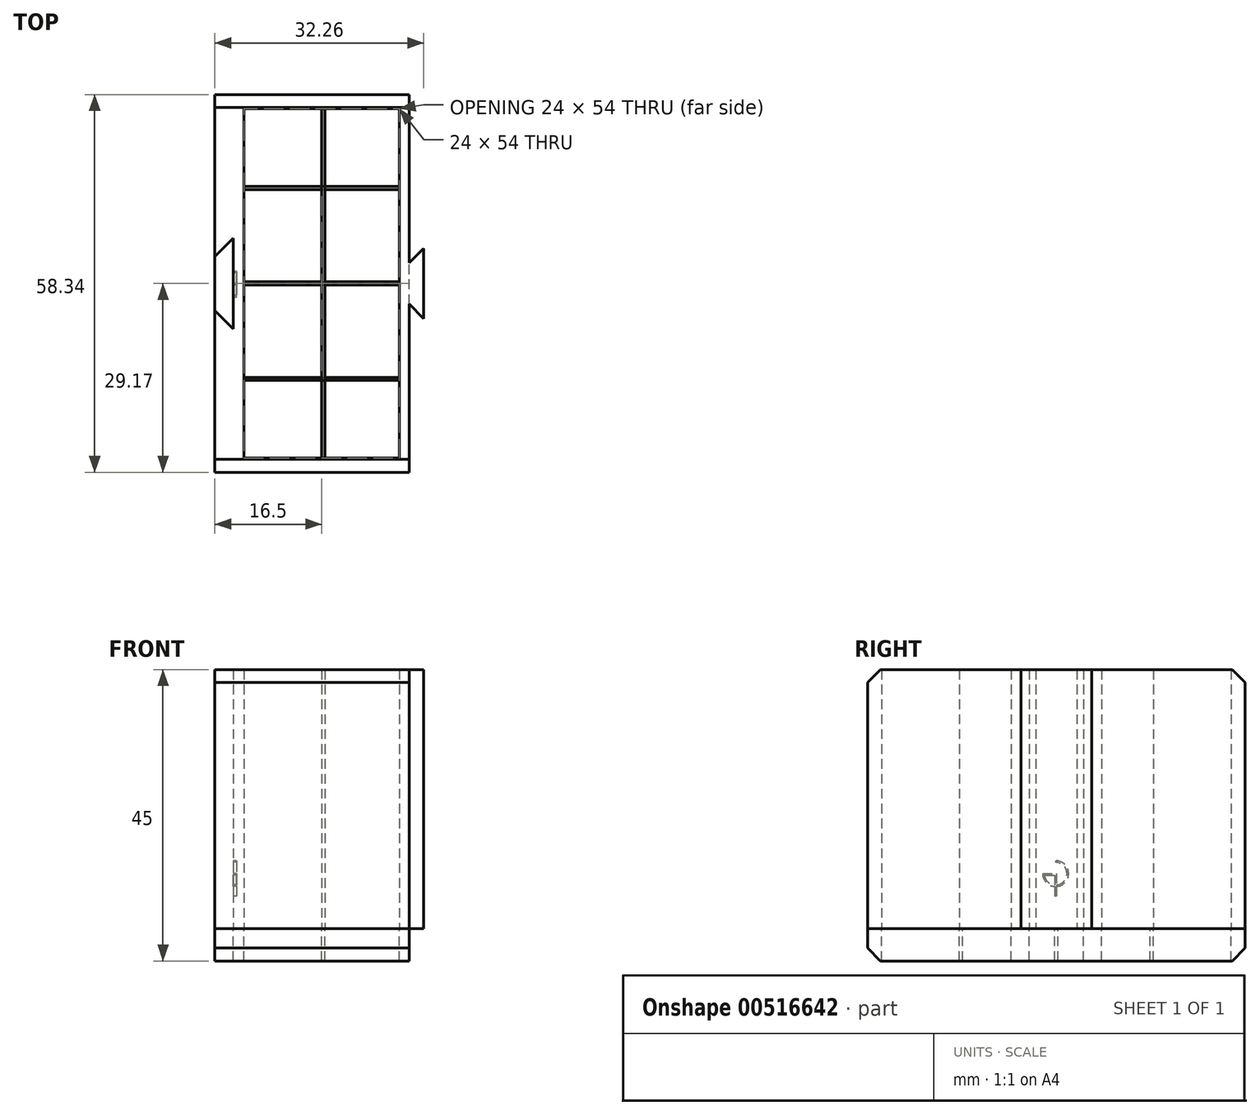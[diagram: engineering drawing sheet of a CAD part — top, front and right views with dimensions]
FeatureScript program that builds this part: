
annotation { "Feature Type Name" : "Feature", "Feature Type Description" : "" }
export const myFeature = defineFeature(function(context is Context, id is Id, definition is map)
    precondition{}
    {
        {
            var Q0;
            Q0=qCreatedBy(makeId("Top.planeOp"),FACE);
            var sketch = newSketch(context, id + "F0", { "sketchPlane" : qUnion([Q0])});
            skLineSegment(sketch, "E0", {"start": v(-15, 4.17) * mm, "end": v(-15, 29.17) * mm});
            skLineSegment(sketch, "E1", {"start": v(-15, 29.17) * mm, "end": v(15, 29.17) * mm});
            skLineSegment(sketch, "E2", {"start": v(15, 29.17) * mm, "end": v(15, 3.17) * mm});
            skLineSegment(sketch, "E3", {"start": v(-15, 4.17) * mm, "end": v(-12.17, 7) * mm});
            skLineSegment(sketch, "E4", {"start": v(-12.17, 7) * mm, "end": v(-12.17, 0) * mm});
            skLineSegment(sketch, "E5", {"start": v(15, 3.17) * mm, "end": v(17.26, 5.43) * mm});
            skLineSegment(sketch, "E6", {"start": v(17.26, 5.43) * mm, "end": v(17.26, -0.57) * mm});
            skLineSegment(sketch, "E7.MirrorCS", {"start": v(-15, -4.17) * mm, "end": v(-12.17, -7) * mm});
            skLineSegment(sketch, "E8.MirrorCS", {"start": v(15, -29.17) * mm, "end": v(15, -3.17) * mm});
            skLineSegment(sketch, "E9.MirrorCS", {"start": v(-12.17, -7) * mm, "end": v(-12.17, 0) * mm});
            skLineSegment(sketch, "E10.MirrorCS", {"start": v(-15, -4.17) * mm, "end": v(-15, -29.17) * mm});
            skLineSegment(sketch, "E11.MirrorCS", {"start": v(17.26, -5.43) * mm, "end": v(17.26, 0.57) * mm});
            skLineSegment(sketch, "E12.MirrorCS", {"start": v(15, -3.17) * mm, "end": v(17.26, -5.43) * mm});
            skLineSegment(sketch, "E13.MirrorCS", {"start": v(-15, -29.17) * mm, "end": v(15, -29.17) * mm});
            skLineSegment(sketch, "E14.bottom", {"start": v(-10.5, 27) * mm, "end": v(13.5, 27) * mm});
            skLineSegment(sketch, "E14.top", {"start": v(-10.5, -27) * mm, "end": v(13.5, -27) * mm});
            skLineSegment(sketch, "E14.left", {"start": v(-10.5, 27) * mm, "end": v(-10.5, -27) * mm});
            skLineSegment(sketch, "E14.right", {"start": v(13.5, 27) * mm, "end": v(13.5, -27) * mm});
            skPoint(sketch, "E14.middle", {"position": v(4, -0.5) * mm});
            skLineSegment(sketch, "E15", {"start": v(-15, 4.17) * mm, "end": v(-15, -4.17) * mm});
            skLineSegment(sketch, "E16", {"start": v(15, -3.17) * mm, "end": v(15, 3.17) * mm});
            skLineSegment(sketch, "E17.bottom", {"start": v(-10.5, 15) * mm, "end": v(13.5, 15) * mm});
            skLineSegment(sketch, "E17.top", {"start": v(-10.5, 14.5) * mm, "end": v(13.5, 14.5) * mm});
            skLineSegment(sketch, "E17.left", {"start": v(-10.5, 15) * mm, "end": v(-10.5, 14.5) * mm});
            skLineSegment(sketch, "E17.right", {"start": v(13.5, 15) * mm, "end": v(13.5, 14.5) * mm});
            skLineSegment(sketch, "E18.bottom", {"start": v(-10.5, -14.5) * mm, "end": v(13.5, -14.5) * mm});
            skLineSegment(sketch, "E18.top", {"start": v(-10.5, -15) * mm, "end": v(13.5, -15) * mm});
            skLineSegment(sketch, "E18.left", {"start": v(-10.5, -14.5) * mm, "end": v(-10.5, -15) * mm});
            skLineSegment(sketch, "E18.right", {"start": v(13.5, -14.5) * mm, "end": v(13.5, -15) * mm});
            skLineSegment(sketch, "E19.bottom", {"start": v(-10.5, 0.25) * mm, "end": v(13.5, 0.25) * mm});
            skLineSegment(sketch, "E19.top", {"start": v(-10.5, -0.25) * mm, "end": v(13.5, -0.25) * mm});
            skLineSegment(sketch, "E19.left", {"start": v(-10.5, 0.25) * mm, "end": v(-10.5, -0.25) * mm});
            skLineSegment(sketch, "E19.right", {"start": v(13.5, 0.25) * mm, "end": v(13.5, -0.25) * mm});
            skLineSegment(sketch, "E20.bottom", {"start": v(1.5, 27) * mm, "end": v(2, 27) * mm});
            skLineSegment(sketch, "E20.top", {"start": v(1.5, -27) * mm, "end": v(2, -27) * mm});
            skLineSegment(sketch, "E20.left", {"start": v(1.5, 27) * mm, "end": v(1.5, -27) * mm});
            skLineSegment(sketch, "E20.right", {"start": v(2, 27) * mm, "end": v(2, -27) * mm});
            skSolve(sketch);
        }
        {
            var Q0;
            Q0=makeQuery(id+"F0.imprint","IMPRINT",FACE,{"disambiguationData":[TD([[makeQuery(id+"F0.imprint","IMPRINT",EDGE,{"derivedFrom":sQuery(id+"F0.wireOp",EDGE,"E5")}),-1.0]])]});
            var Q1;
            Q1=makeQuery(id+"F0.imprint","IMPRINT",FACE,{"disambiguationData":[TD([[makeQuery(id+"F0.imprint","IMPRINT",EDGE,{"derivedFrom":sQuery(id+"F0.wireOp",EDGE,"E0")}),-1.0]])]});
            var Q2;
            {var subQ0=sQuery(id+"F0.wireOp",EDGE,"E20.left");var subQ1=sQuery(id+"F0.wireOp",EDGE,"E18.bottom");var subQ2=makeQuery(id+"F0.imprint","INTERSECT",VERTEX,{"derivedFrom":[subQ1,subQ0]});Q2=makeQuery(id+"F0.imprint","IMPRINT",FACE,{"disambiguationData":[TD([[makeQuery(id+"F0.imprint","IMPRINT",EDGE,{"disambiguationData":[TD([[subQ2,-1.0]])],"derivedFrom":subQ1}),1.0]])]});}
            var Q3;
            {var subQ5=sQuery(id+"F0.wireOp",EDGE,"E20.bottom");Q3=makeQuery(id+"F0.imprint","IMPRINT",FACE,{"disambiguationData":[TD([[makeQuery(id+"F0.imprint","IMPRINT",EDGE,{"derivedFrom":subQ5}),-1.0]])]});}
            var Q4;
            {var subQ0=sQuery(id+"F0.wireOp",EDGE,"E17.right");Q4=makeQuery(id+"F0.imprint","IMPRINT",FACE,{"disambiguationData":[TD([[makeQuery(id+"F0.imprint","IMPRINT",EDGE,{"derivedFrom":subQ0}),-1.0]])]});}
            var Q5;
            {var subQ0=sQuery(id+"F0.wireOp",EDGE,"E19.left");Q5=makeQuery(id+"F0.imprint","IMPRINT",FACE,{"disambiguationData":[TD([[makeQuery(id+"F0.imprint","IMPRINT",EDGE,{"derivedFrom":subQ0}),1.0]])]});}
            var Q6;
            {var subQ0=sQuery(id+"F0.wireOp",EDGE,"E19.right");Q6=makeQuery(id+"F0.imprint","IMPRINT",FACE,{"disambiguationData":[TD([[makeQuery(id+"F0.imprint","IMPRINT",EDGE,{"derivedFrom":subQ0}),-1.0]])]});}
            var Q7;
            {var subQ0=sQuery(id+"F0.wireOp",EDGE,"E18.right");Q7=makeQuery(id+"F0.imprint","IMPRINT",FACE,{"disambiguationData":[TD([[makeQuery(id+"F0.imprint","IMPRINT",EDGE,{"derivedFrom":subQ0}),-1.0]])]});}
            var Q8;
            {var subQ0=sQuery(id+"F0.wireOp",EDGE,"E18.left");Q8=makeQuery(id+"F0.imprint","IMPRINT",FACE,{"disambiguationData":[TD([[makeQuery(id+"F0.imprint","IMPRINT",EDGE,{"derivedFrom":subQ0}),1.0]])]});}
            var Q9;
            {var subQ0=sQuery(id+"F0.wireOp",EDGE,"E17.left");Q9=makeQuery(id+"F0.imprint","IMPRINT",FACE,{"disambiguationData":[TD([[makeQuery(id+"F0.imprint","IMPRINT",EDGE,{"derivedFrom":subQ0}),1.0]])]});}
            var Q10;
            {var subQ0=sQuery(id+"F0.wireOp",EDGE,"E20.left");var subQ1=sQuery(id+"F0.wireOp",EDGE,"E17.top");var subQ2=makeQuery(id+"F0.imprint","INTERSECT",VERTEX,{"derivedFrom":[subQ1,subQ0]});Q10=makeQuery(id+"F0.imprint","IMPRINT",FACE,{"disambiguationData":[TD([[makeQuery(id+"F0.imprint","IMPRINT",EDGE,{"disambiguationData":[TD([[subQ2,-1.0]])],"derivedFrom":subQ1}),-1.0]])]});}
            var Q11;
            {var subQ5=sQuery(id+"F0.wireOp",EDGE,"E20.top");Q11=makeQuery(id+"F0.imprint","IMPRINT",FACE,{"disambiguationData":[TD([[makeQuery(id+"F0.imprint","IMPRINT",EDGE,{"derivedFrom":subQ5}),1.0]])]});}
            var Q12;
            {var subQ0=sQuery(id+"F0.wireOp",EDGE,"E20.left");var subQ1=sQuery(id+"F0.wireOp",EDGE,"E18.bottom");var subQ2=makeQuery(id+"F0.imprint","INTERSECT",VERTEX,{"derivedFrom":[subQ1,subQ0]});Q12=makeQuery(id+"F0.imprint","IMPRINT",FACE,{"disambiguationData":[TD([[makeQuery(id+"F0.imprint","IMPRINT",EDGE,{"disambiguationData":[TD([[subQ2,-1.0]])],"derivedFrom":subQ1}),-1.0]])]});}
            var Q13;
            {var subQ0=sQuery(id+"F0.wireOp",EDGE,"E20.left");var subQ1=sQuery(id+"F0.wireOp",EDGE,"E19.bottom");var subQ2=makeQuery(id+"F0.imprint","INTERSECT",VERTEX,{"derivedFrom":[subQ1,subQ0]});Q13=makeQuery(id+"F0.imprint","IMPRINT",FACE,{"disambiguationData":[TD([[makeQuery(id+"F0.imprint","IMPRINT",EDGE,{"disambiguationData":[TD([[subQ2,-1.0]])],"derivedFrom":subQ1}),-1.0]])]});}
            var Q14;
            {var subQ0=sQuery(id+"F0.wireOp",EDGE,"E20.left");var subQ1=sQuery(id+"F0.wireOp",EDGE,"E17.bottom");var subQ2=makeQuery(id+"F0.imprint","INTERSECT",VERTEX,{"derivedFrom":[subQ1,subQ0]});Q14=makeQuery(id+"F0.imprint","IMPRINT",FACE,{"disambiguationData":[TD([[makeQuery(id+"F0.imprint","IMPRINT",EDGE,{"disambiguationData":[TD([[subQ2,-1.0]])],"derivedFrom":subQ1}),-1.0]])]});}
            extrude(context, id + "F1", {"entities" : qUnion([Q0, Q1, Q2, Q3, Q4, Q5, Q6, Q7, Q8, Q9, Q10, Q11, Q12, Q13, Q14]), "depth" : 40 * mm, "offsetDistance" : 25 * mm});
        }
        {
            var Q0;
            Q0=makeQuery(id+"F0.imprint","IMPRINT",FACE,{"disambiguationData":[TD([[makeQuery(id+"F0.imprint","IMPRINT",EDGE,{"derivedFrom":sQuery(id+"F0.wireOp",EDGE,"E0")}),-1.0]])]});
            var Q1;
            Q1=makeQuery(id+"F0.imprint","IMPRINT",FACE,{"disambiguationData":[TD([[makeQuery(id+"F0.imprint","IMPRINT",EDGE,{"derivedFrom":sQuery(id+"F0.wireOp",EDGE,"E3")}),-1.0]])]});
            var Q2;
            {var subQ5=sQuery(id+"F0.wireOp",EDGE,"E20.top");Q2=makeQuery(id+"F0.imprint","IMPRINT",FACE,{"disambiguationData":[TD([[makeQuery(id+"F0.imprint","IMPRINT",EDGE,{"derivedFrom":subQ5}),1.0]])]});}
            var Q3;
            {var subQ0=sQuery(id+"F0.wireOp",EDGE,"E14.right");var subQ1=sQuery(id+"F0.wireOp",EDGE,"E14.top");var subQ2=makeQuery(id+"F0.imprint","INTERSECT",VERTEX,{"derivedFrom":[subQ1,subQ0]});Q3=makeQuery(id+"F0.imprint","IMPRINT",FACE,{"disambiguationData":[TD([[makeQuery(id+"F0.imprint","IMPRINT",EDGE,{"disambiguationData":[TD([[subQ2,1.0]])],"derivedFrom":subQ1}),1.0]])]});}
            var Q4;
            {var subQ0=sQuery(id+"F0.wireOp",EDGE,"E14.left");var subQ1=sQuery(id+"F0.wireOp",EDGE,"E14.top");var subQ2=makeQuery(id+"F0.imprint","INTERSECT",VERTEX,{"derivedFrom":[subQ1,subQ0]});Q4=makeQuery(id+"F0.imprint","IMPRINT",FACE,{"disambiguationData":[TD([[makeQuery(id+"F0.imprint","IMPRINT",EDGE,{"disambiguationData":[TD([[subQ2,-1.0]])],"derivedFrom":subQ1}),1.0]])]});}
            var Q5;
            {var subQ0=sQuery(id+"F0.wireOp",EDGE,"E18.left");Q5=makeQuery(id+"F0.imprint","IMPRINT",FACE,{"disambiguationData":[TD([[makeQuery(id+"F0.imprint","IMPRINT",EDGE,{"derivedFrom":subQ0}),1.0]])]});}
            var Q6;
            {var subQ0=sQuery(id+"F0.wireOp",EDGE,"E20.left");var subQ1=sQuery(id+"F0.wireOp",EDGE,"E18.bottom");var subQ2=makeQuery(id+"F0.imprint","INTERSECT",VERTEX,{"derivedFrom":[subQ1,subQ0]});Q6=makeQuery(id+"F0.imprint","IMPRINT",FACE,{"disambiguationData":[TD([[makeQuery(id+"F0.imprint","IMPRINT",EDGE,{"disambiguationData":[TD([[subQ2,-1.0]])],"derivedFrom":subQ1}),-1.0]])]});}
            var Q7;
            {var subQ0=sQuery(id+"F0.wireOp",EDGE,"E20.left");var subQ1=sQuery(id+"F0.wireOp",EDGE,"E18.bottom");var subQ2=makeQuery(id+"F0.imprint","INTERSECT",VERTEX,{"derivedFrom":[subQ1,subQ0]});Q7=makeQuery(id+"F0.imprint","IMPRINT",FACE,{"disambiguationData":[TD([[makeQuery(id+"F0.imprint","IMPRINT",EDGE,{"disambiguationData":[TD([[subQ2,-1.0]])],"derivedFrom":subQ1}),1.0]])]});}
            var Q8;
            {var subQ0=sQuery(id+"F0.wireOp",EDGE,"E18.bottom");var subQ5=sQuery(id+"F0.wireOp",EDGE,"E20.left");var subQ6=makeQuery(id+"F0.imprint","INTERSECT",VERTEX,{"derivedFrom":[subQ0,subQ5]});Q8=makeQuery(id+"F0.imprint","IMPRINT",FACE,{"disambiguationData":[TD([[makeQuery(id+"F0.imprint","IMPRINT",EDGE,{"disambiguationData":[TD([[subQ6,1.0]])],"derivedFrom":subQ5}),-1.0]])]});}
            var Q9;
            {var subQ0=sQuery(id+"F0.wireOp",EDGE,"E18.bottom");var subQ5=sQuery(id+"F0.wireOp",EDGE,"E20.right");var subQ7=makeQuery(id+"F0.imprint","INTERSECT",VERTEX,{"derivedFrom":[subQ0,subQ5]});Q9=makeQuery(id+"F0.imprint","IMPRINT",FACE,{"disambiguationData":[TD([[makeQuery(id+"F0.imprint","IMPRINT",EDGE,{"disambiguationData":[TD([[subQ7,1.0]])],"derivedFrom":subQ5}),1.0]])]});}
            var Q10;
            {var subQ0=sQuery(id+"F0.wireOp",EDGE,"E17.top");var subQ5=sQuery(id+"F0.wireOp",EDGE,"E20.right");var subQ6=makeQuery(id+"F0.imprint","INTERSECT",VERTEX,{"derivedFrom":[subQ0,subQ5]});Q10=makeQuery(id+"F0.imprint","IMPRINT",FACE,{"disambiguationData":[TD([[makeQuery(id+"F0.imprint","IMPRINT",EDGE,{"disambiguationData":[TD([[subQ6,-1.0]])],"derivedFrom":subQ5}),1.0]])]});}
            var Q11;
            {var subQ0=sQuery(id+"F0.wireOp",EDGE,"E17.top");var subQ5=sQuery(id+"F0.wireOp",EDGE,"E20.left");var subQ7=makeQuery(id+"F0.imprint","INTERSECT",VERTEX,{"derivedFrom":[subQ0,subQ5]});Q11=makeQuery(id+"F0.imprint","IMPRINT",FACE,{"disambiguationData":[TD([[makeQuery(id+"F0.imprint","IMPRINT",EDGE,{"disambiguationData":[TD([[subQ7,-1.0]])],"derivedFrom":subQ5}),-1.0]])]});}
            var Q12;
            {var subQ0=sQuery(id+"F0.wireOp",EDGE,"E20.left");var subQ1=sQuery(id+"F0.wireOp",EDGE,"E19.bottom");var subQ2=makeQuery(id+"F0.imprint","INTERSECT",VERTEX,{"derivedFrom":[subQ1,subQ0]});Q12=makeQuery(id+"F0.imprint","IMPRINT",FACE,{"disambiguationData":[TD([[makeQuery(id+"F0.imprint","IMPRINT",EDGE,{"disambiguationData":[TD([[subQ2,-1.0]])],"derivedFrom":subQ1}),-1.0]])]});}
            var Q13;
            {var subQ0=sQuery(id+"F0.wireOp",EDGE,"E20.left");var subQ1=sQuery(id+"F0.wireOp",EDGE,"E17.top");var subQ2=makeQuery(id+"F0.imprint","INTERSECT",VERTEX,{"derivedFrom":[subQ1,subQ0]});Q13=makeQuery(id+"F0.imprint","IMPRINT",FACE,{"disambiguationData":[TD([[makeQuery(id+"F0.imprint","IMPRINT",EDGE,{"disambiguationData":[TD([[subQ2,-1.0]])],"derivedFrom":subQ1}),-1.0]])]});}
            var Q14;
            {var subQ0=sQuery(id+"F0.wireOp",EDGE,"E17.right");Q14=makeQuery(id+"F0.imprint","IMPRINT",FACE,{"disambiguationData":[TD([[makeQuery(id+"F0.imprint","IMPRINT",EDGE,{"derivedFrom":subQ0}),-1.0]])]});}
            var Q15;
            {var subQ0=sQuery(id+"F0.wireOp",EDGE,"E20.left");var subQ1=sQuery(id+"F0.wireOp",EDGE,"E17.bottom");var subQ2=makeQuery(id+"F0.imprint","INTERSECT",VERTEX,{"derivedFrom":[subQ1,subQ0]});Q15=makeQuery(id+"F0.imprint","IMPRINT",FACE,{"disambiguationData":[TD([[makeQuery(id+"F0.imprint","IMPRINT",EDGE,{"disambiguationData":[TD([[subQ2,-1.0]])],"derivedFrom":subQ1}),-1.0]])]});}
            var Q16;
            {var subQ0=sQuery(id+"F0.wireOp",EDGE,"E17.left");Q16=makeQuery(id+"F0.imprint","IMPRINT",FACE,{"disambiguationData":[TD([[makeQuery(id+"F0.imprint","IMPRINT",EDGE,{"derivedFrom":subQ0}),1.0]])]});}
            var Q17;
            {var subQ0=sQuery(id+"F0.wireOp",EDGE,"E14.left");var subQ1=sQuery(id+"F0.wireOp",EDGE,"E14.bottom");var subQ2=makeQuery(id+"F0.imprint","INTERSECT",VERTEX,{"derivedFrom":[subQ1,subQ0]});Q17=makeQuery(id+"F0.imprint","IMPRINT",FACE,{"disambiguationData":[TD([[makeQuery(id+"F0.imprint","IMPRINT",EDGE,{"disambiguationData":[TD([[subQ2,-1.0]])],"derivedFrom":subQ1}),-1.0]])]});}
            var Q18;
            {var subQ0=sQuery(id+"F0.wireOp",EDGE,"E14.right");var subQ1=sQuery(id+"F0.wireOp",EDGE,"E14.bottom");var subQ2=makeQuery(id+"F0.imprint","INTERSECT",VERTEX,{"derivedFrom":[subQ1,subQ0]});Q18=makeQuery(id+"F0.imprint","IMPRINT",FACE,{"disambiguationData":[TD([[makeQuery(id+"F0.imprint","IMPRINT",EDGE,{"disambiguationData":[TD([[subQ2,1.0]])],"derivedFrom":subQ1}),-1.0]])]});}
            var Q19;
            {var subQ5=sQuery(id+"F0.wireOp",EDGE,"E20.bottom");Q19=makeQuery(id+"F0.imprint","IMPRINT",FACE,{"disambiguationData":[TD([[makeQuery(id+"F0.imprint","IMPRINT",EDGE,{"derivedFrom":subQ5}),-1.0]])]});}
            var Q20;
            {var subQ0=sQuery(id+"F0.wireOp",EDGE,"E19.left");Q20=makeQuery(id+"F0.imprint","IMPRINT",FACE,{"disambiguationData":[TD([[makeQuery(id+"F0.imprint","IMPRINT",EDGE,{"derivedFrom":subQ0}),1.0]])]});}
            var Q21;
            {var subQ0=sQuery(id+"F0.wireOp",EDGE,"E19.right");Q21=makeQuery(id+"F0.imprint","IMPRINT",FACE,{"disambiguationData":[TD([[makeQuery(id+"F0.imprint","IMPRINT",EDGE,{"derivedFrom":subQ0}),-1.0]])]});}
            var Q22;
            {var subQ0=sQuery(id+"F0.wireOp",EDGE,"E18.right");Q22=makeQuery(id+"F0.imprint","IMPRINT",FACE,{"disambiguationData":[TD([[makeQuery(id+"F0.imprint","IMPRINT",EDGE,{"derivedFrom":subQ0}),-1.0]])]});}
            extrude(context, id + "F2", {"entities" : qUnion([Q0, Q1, Q2, Q3, Q4, Q5, Q6, Q7, Q8, Q9, Q10, Q11, Q12, Q13, Q14, Q15, Q16, Q17, Q18, Q19, Q20, Q21, Q22]), "operationType" : NewBodyOperationType.ADD, "oppositeDirection" : true, "depth" : 5 * mm, "offsetDistance" : 25 * mm});
        }
        {
            var Q0;
            Q0=makeQuery(id+"F2.opExtrude","CAP_EDGE",EDGE,{"disambiguationData":[OSD([sQuery(id+"F0.wireOp",EDGE,"E13.MirrorCS")])],"isStart":false});
            var Q1;
            Q1=makeQuery(id+"F2.opExtrude","CAP_EDGE",EDGE,{"disambiguationData":[OSD([sQuery(id+"F0.wireOp",EDGE,"E1")])],"isStart":false});
            var Q2;
            Q2=makeQuery(id+"F1.opExtrude","CAP_EDGE",EDGE,{"disambiguationData":[OSD([sQuery(id+"F0.wireOp",EDGE,"E13.MirrorCS")])],"isStart":false});
            var Q3;
            Q3=makeQuery(id+"F1.opExtrude","CAP_EDGE",EDGE,{"disambiguationData":[OSD([sQuery(id+"F0.wireOp",EDGE,"E1")])],"isStart":false});
            chamfer(context, id + "F3", {"entities" : qUnion([Q0, Q1, Q2, Q3]), "width" : 2 * mm, "tangentPropagation" : true});
        }
        {
            var Q0;
            Q0=makeQuery(id+"F1.opExtrude","SWEPT_FACE",FACE,{"disambiguationData":[OSD([sQuery(id+"F0.wireOp",EDGE,"E4"),sQuery(id+"F0.wireOp",EDGE,"E9.MirrorCS")])]});
            var sketch = newSketch(context, id + "F4", { "sketchPlane" : qUnion([Q0])});
            skLineSegment(sketch, "E21.bottom", {"start": v(0.12, 10.5) * mm, "end": v(2.12, 10.5) * mm, "construction": true});
            skLineSegment(sketch, "E21.top", {"start": v(0.12, 8.5) * mm, "end": v(2.12, 8.5) * mm, "construction": true});
            skLineSegment(sketch, "E21.left", {"start": v(0.12, 10.5) * mm, "end": v(0.12, 8.5) * mm, "construction": true});
            skLineSegment(sketch, "E21.right", {"start": v(2.12, 10.5) * mm, "end": v(2.12, 8.5) * mm, "construction": true});
            skArc(sketch, "E22", {"start": v(0.12, 10.5) * mm, "mid": v(-1.3, 7.09) * mm, "end": v(2.12, 8.5) * mm});
            skLineSegment(sketch, "E23", {"start": v(0.12, 10.5) * mm, "end": v(0.12, 10.25) * mm});
            skLineSegment(sketch, "E24", {"start": v(2.12, 8.5) * mm, "end": v(1.87, 8.5) * mm});
            skArc(sketch, "E25", {"start": v(0.12, 10.25) * mm, "mid": v(-1.12, 7.26) * mm, "end": v(1.87, 8.5) * mm});
            skLineSegment(sketch, "E26", {"start": v(1.87, 8.5) * mm, "end": v(0, 8.5) * mm});
            skLineSegment(sketch, "E27", {"start": v(0, 8.5) * mm, "end": v(0, 5) * mm});
            skLineSegment(sketch, "E28", {"start": v(0, 5) * mm, "end": v(0.25, 5) * mm});
            skLineSegment(sketch, "E29", {"start": v(1.85, 8.25) * mm, "end": v(0.25, 8.25) * mm});
            skLineSegment(sketch, "E30", {"start": v(0.25, 8.25) * mm, "end": v(0.25, 5) * mm});
            skSolve(sketch);
        }
        {
            var Q0;
            {var subQ0=sQuery(id+"F4.wireOp",EDGE,"E23");Q0=makeQuery(id+"F4.imprint","IMPRINT",FACE,{"disambiguationData":[TD([[makeQuery(id+"F4.imprint","IMPRINT",EDGE,{"derivedFrom":subQ0}),-1.0]])]});}
            var Q1;
            {var subQ1=sQuery(id+"F4.wireOp",EDGE,"E26");Q1=makeQuery(id+"F4.imprint","IMPRINT",FACE,{"disambiguationData":[TD([[makeQuery(id+"F4.imprint","IMPRINT",EDGE,{"derivedFrom":subQ1}),1.0]])]});}
            var Q2;
            {var subQ1=sQuery(id+"F4.wireOp",EDGE,"E24");Q2=makeQuery(id+"F4.imprint","IMPRINT",FACE,{"disambiguationData":[TD([[makeQuery(id+"F4.imprint","IMPRINT",EDGE,{"derivedFrom":subQ1}),1.0]])]});}
            var Q3;
            {var subQ0=sQuery(id+"F4.wireOp",EDGE,"E27");var subQ1=sQuery(id+"F4.wireOp",EDGE,"E22");var subQ2=makeQuery(id+"F4.imprint","INTERSECT",VERTEX,{"derivedFrom":[subQ1,subQ0]});Q3=makeQuery(id+"F4.imprint","IMPRINT",FACE,{"disambiguationData":[TD([[makeQuery(id+"F4.imprint","IMPRINT",EDGE,{"disambiguationData":[TD([[subQ2,-1.0]])],"derivedFrom":subQ1}),1.0]])]});}
            var Q4;
            {var subQ5=sQuery(id+"F4.wireOp",EDGE,"E28");Q4=makeQuery(id+"F4.imprint","IMPRINT",FACE,{"disambiguationData":[TD([[makeQuery(id+"F4.imprint","IMPRINT",EDGE,{"derivedFrom":subQ5}),1.0]])]});}
            extrude(context, id + "F5", {"entities" : qUnion([Q0, Q1, Q2, Q3, Q4]), "operationType" : NewBodyOperationType.REMOVE, "oppositeDirection" : true, "depth" : .5 * mm, "offsetDistance" : 25 * mm});
        }
    });
